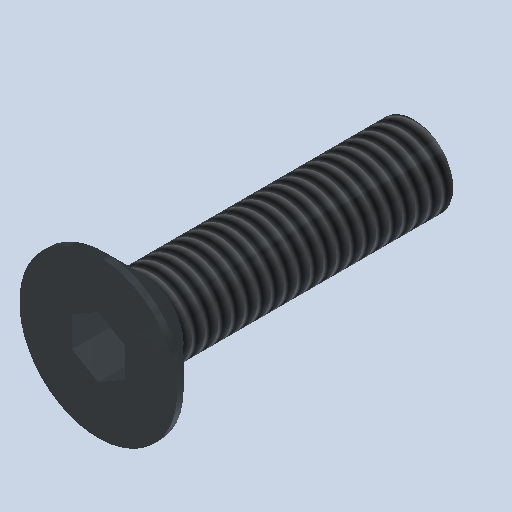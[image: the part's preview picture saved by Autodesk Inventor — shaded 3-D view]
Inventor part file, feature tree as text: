
AUTODESK INVENTOR PART (.ipt)
format: ipt  version: 2022 (Build 260153000, 153)  size: 174,080 bytes
history: native  units: mm
features: extrude x3, sketch x3, other x1, thread x1, chamfer x1
ambient origin geometry x8: Origin, YZ Plane, XZ Plane, XY Plane, X Axis, Y Axis, Z Axis, Center Point
bodies: Body1 (feature_tree)
feature tree (9):
  other  "ソリッド1"
  extrude  "押し出し1"  Depth=3.0mm
  thread  "ねじ1"
  extrude  "押し出し2"  Depth=12.0mm TaperAngle=0.0deg
  chamfer  "面取り1"  Distance=10.0mm
  extrude  "押し出し3"  Depth=6.0mm
  sketch  "スケッチ1"
  sketch  "スケッチ2"
  sketch  "スケッチ3"
